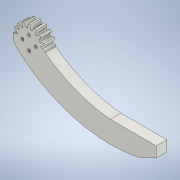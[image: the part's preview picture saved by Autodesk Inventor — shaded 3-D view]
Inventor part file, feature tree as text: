
AUTODESK INVENTOR PART (.ipt)
format: ipt  version: 2020 (Build 240168000, 168)  size: 360,448 bytes
history: native  units: mm (DEFAULTED — no unit token found)
features: sketch x13, extrude x12, plane x3, other x3
ambient origin geometry x8: Origin, YZ Plane, XZ Plane, XY Plane, X Axis, Y Axis, Z Axis, Center Point
bodies: Solid1 (feature_tree)
feature tree (31):
  extrude  "Extrusion1"  Depth=12.7mm TaperAngle=0.0deg
  plane  "Work Plane1"
  plane  "Work Plane2"
  plane  "Work Plane3"
  other  "Spur Gear"
  extrude  "Extrusion2"  Depth=76.2mm TaperAngle=0.0deg
  sketch  "Sketch4"  dims[d14=0.0mm d15=34.076615mm]
  extrude  "Extrusion3"  TaperAngle=0.0deg  [1 undecoded]
  extrude  "Extrusion4"  Depth=34.076615mm
  extrude  "Extrusion5"  TaperAngle=0.0deg  [1 undecoded]
  extrude  "Extrusion6"  Depth=34.076615mm
  extrude  "Extrusion7"  Depth=31.6611mm
  extrude  "Extrusion9"  Depth=12.7mm TaperAngle=0.0deg
  extrude  "Extrusion10"  Depth=12.7mm
  extrude  "Extrusion11"  Depth=12.7mm
  extrude  "Extrusion13"  Depth=12.7mm TaperAngle=0.0deg
  extrude  "Extrusion15"  Depth=12.7mm TaperAngle=0.0deg
  sketch  "Sketch1"  dims[d0=38.305046mm d1=12.7mm d2=0.0mm]
  sketch  "Sketch2"  dims[d3=34.076615mm d4=76.2mm d5=0.0mm]
  other  "Srf1"
  sketch  "Sketch3"  dims[d6=0.0mm d7=1.963495mm d9=0.0mm]
  sketch  "Sketch6"  dims[d16=0.0mm d17=0.0mm]
  sketch  "Sketch7"  dims[d18=0.0mm d19=34.076615mm]
  sketch  "Sketch8"  dims[d25=25.4mm d26=0.0mm d27=31.6611mm]
  sketch  "Sketch9"  dims[d28=127.0mm d29=12.7mm d30=0.0mm]
  sketch  "Sketch11"  dims[d31=12.7mm d32=0.0mm d33=38.1mm]
  sketch  "Sketch12"  dims[d34=12.7mm d35=25.4mm]
  sketch  "Sketch13"  dims[d36=12.7mm d37=0.0mm d38=12.7mm d39=0.0mm]
  sketch  "Sketch15"  dims[d40=12.7mm d41=0.0mm d48=12.7mm d49=0.0mm]
  sketch  "Sketch17"  dims[d50=12.7mm d51=0.0mm d52=12.7mm d53=0.0mm d60=12.7mm d61=0.0mm d65=12.7mm d66=0.0mm d67=16.002mm d68=3.5814mm d69=3.5814mm d70=3.5814mm d71=3.5814mm d24=12.7mm]
  other  "Pitch Diameter"
note: 2 required parameter values undecoded (feature->parameter linkage not recoverable at this tier; creation-order binding heuristic only, values carry confidence <= 0.55)
